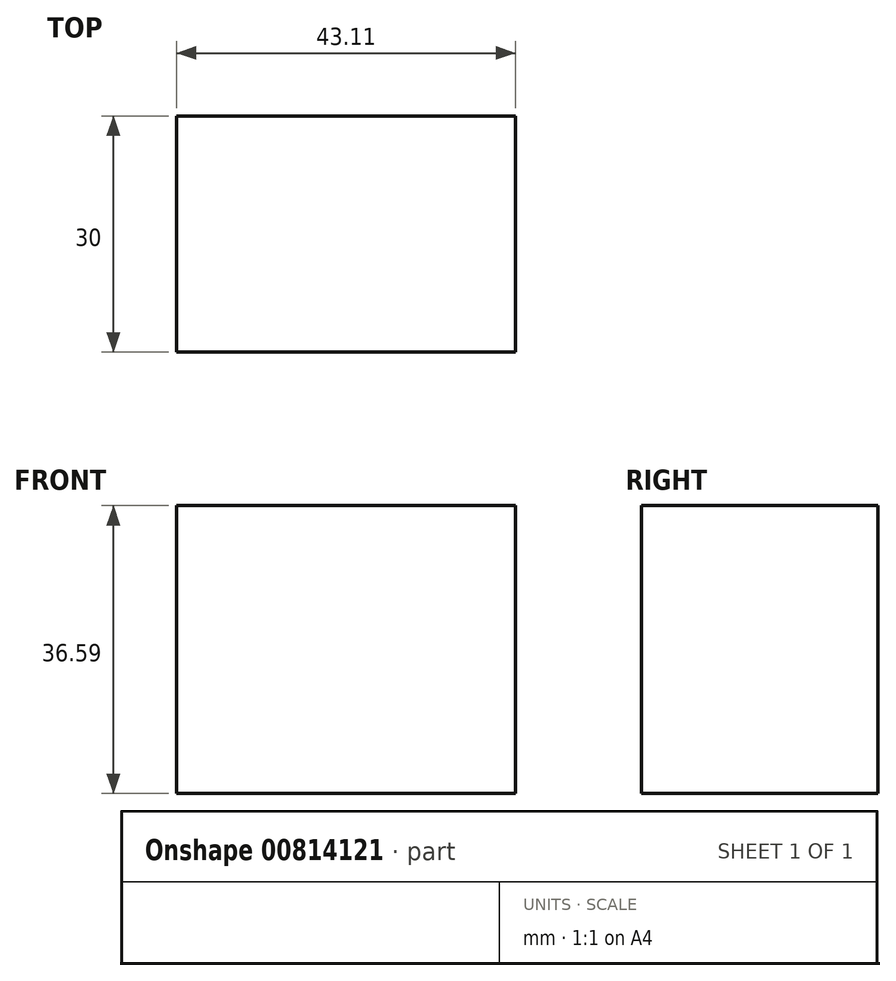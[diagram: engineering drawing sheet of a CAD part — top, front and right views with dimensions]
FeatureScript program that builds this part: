
annotation { "Feature Type Name" : "Feature", "Feature Type Description" : "" }
export const myFeature = defineFeature(function(context is Context, id is Id, definition is map)
    precondition{}
    {
        {
            var Q0;
            Q0=qCreatedBy(makeId("Front.planeOp"),FACE);
            var sketch = newSketch(context, id + "F0", { "sketchPlane" : qUnion([Q0])});
            skLineSegment(sketch, "E0.bottom", {"start": v(0, 0) * mm, "end": v(43.1, 0) * mm});
            skLineSegment(sketch, "E0.top", {"start": v(0, 36.59) * mm, "end": v(43.1, 36.59) * mm});
            skLineSegment(sketch, "E0.left", {"start": v(0, 0) * mm, "end": v(0, 36.59) * mm});
            skLineSegment(sketch, "E0.right", {"start": v(43.1, 0) * mm, "end": v(43.1, 36.59) * mm});
            skSolve(sketch);
        }
        {
            var Q0;
            Q0=makeQuery(id+"F0.imprint","IMPRINT",FACE,{"disambiguationData":[TD([[makeQuery(id+"F0.imprint","IMPRINT",EDGE,{"derivedFrom":sQuery(id+"F0.wireOp",EDGE,"E0.bottom")}),1.0]])]});
            extrude(context, id + "F1", {"entities" : qUnion([Q0]), "oppositeDirection" : true, "depth" : 30 * mm, "offsetDistance" : 25 * mm});
        }
        {
            var Q0;
            Q0=qCreatedBy(makeId("Front.planeOp"),FACE);
            var sketch = newSketch(context, id + "F2", { "sketchPlane" : qUnion([Q0])});
            skArc(sketch, "E1", {"start": v(0, 13.8) * mm, "mid": v(-13.8, 0) * mm, "end": v(0, -13.8) * mm});
            skSolve(sketch);
        }
        {
            var Q0;
            Q0=sQuery(id+"F2.wireOp",EDGE,"E1");
            var Q1;
            Q1=makeQuery(id+"F1.opExtrude","CAP_EDGE",EDGE,{"disambiguationData":[OSD([sQuery(id+"F0.wireOp",EDGE,"E0.left")])],"isStart":true});
            revolve(context, id + "F3", {"bodyType" : ToolBodyType.SURFACE, "surfaceOperationType" : NewSurfaceOperationType.NEW, "surfaceEntities" : qUnion([Q0]), "axis" : qUnion([Q1]), "revolveType" : RevolveType.FULL});
        }
        {
            var Q0;
            Q0=qCreatedBy(makeId("Front.planeOp"),FACE);
            var sketch = newSketch(context, id + "F4", { "sketchPlane" : qUnion([Q0])});
            skLineSegment(sketch, "E2", {"start": v(0, 0) * mm, "end": v(89.46, 72.23) * mm});
            skSolve(sketch);
        }
    });
